# Revit family: BISLEY_CLK_Lockers
name_source: partatom
category: Furniture
revit_build: Autodesk Revit 2018 (Build: 20180423_1000(x64)
units: mm (PartAtom-declared; Revit-internal decimal feet)

## family parameters
Always vertical = Yes
Cut with Voids When Loaded = No
OmniClass Number = 23.40.20.00
OmniClass Title = General Furniture and Specialties
Room Calculation Point = No
Shared = No
Work Plane-Based = No

## types (10) — shared parameters
1st = Yes
5th Door Height = 282 mm
6th Door Height = 282 mm
Category = Furniture
Compliance Standards Certification = BS EN 14073 2004 Part 2 & 3, BS EN 14074, BS 4875 1998 Part 7 level 4, DIN 4554/485
Finish = Powder Coated
Manufacturer = BISLEY
Material = Steel
Model = CLK Lockers
Range = CLK Lockers
Routine Maintenance = We recommend you clean your unit with warm water and a mild detergent solution. A damp cloth can be used to remove dust particles.
URL = www.bisley.com
Uniclass 2015 Code = PR_40_30_48
Uniclass2015Title = Shelves and Storage Units
Uniclass2015Version = V1.1
Warranty = 5 Years from date of purchase
Width = 305 mm  [stored 1.00066 ft]

## per-type parameters (varying)
| type | 1st Door height | 2nd | 2nd Doors Height | 3rd | 3rd Door Height | 4th | 4th Door height | 5th | 6th | Code | Depth | Description | Dimensions | Height | Model Reference | Product Information |
| CLK186 | 282 mm | Yes | 282 mm | Yes | 282 mm | Yes | 282 mm | Yes | Yes |  | 457 mm  [stored 1.49934 ft] | 6 Door Locker | 1802 x 305 x 457 mm | 1802 mm  [stored 5.91207 ft] | CLK186 | 6 Door Locker |
| CLK121 | 1699 mm  [stored 5.57415 ft] | No | 282 mm | No | 282 mm | No | 282 mm | No | No |  | 305 mm  [stored 1.00066 ft] | 1 Door Locker | 529 x 305 x 305 mm | 1802 mm  [stored 5.91207 ft] | CLK121 | 1 Door Locker |
| CLK181 | 1699 mm  [stored 5.57415 ft] | No | 282 mm | No | 282 mm | No | 282 mm | No | No | CLK181 | 457 mm  [stored 1.49934 ft] | 1 Door Locker | 1802 x 305 x 457 mm | 1802 mm  [stored 5.91207 ft] | "CLK181" | 1 Door Locker |
| CLK121C | 426 mm  [stored 1.39764 ft] | No | 282 mm | No | 282 mm | No | 282 mm | No | No |  | 305 mm  [stored 1.00066 ft] |  | 529 x 305 x 305 mm | 529 mm  [stored 1.73556 ft] | CLK121C |  |
| CLK181C | 426 mm  [stored 1.39764 ft] | No | 282 mm | No | 282 mm | No | 282 mm | No | No | CLK181C | 457 mm  [stored 1.49934 ft] | 1 Door Cube | 529 x 305 x 457 mm | 529 mm  [stored 1.73556 ft] | CLK181C | 1 Door Cube |
| CLK122 | 849 mm | Yes | 849 mm | No | 282 mm | No | 282 mm | No | No | CLK122 | 305 mm  [stored 1.00066 ft] | 2 Door Locker | 1802 x 305 x 305 mm | 1802 mm  [stored 5.91207 ft] | CLK122 | 2 Door Locker |
| CLK124 | 424 mm | Yes | 424 mm | Yes | 424 mm | Yes | 424 mm | No | No | CLK124 | 305 mm  [stored 1.00066 ft] | 4 Door Locker | 1802 x 305 x 305 mm | 1802 mm  [stored 5.91207 ft] | CLK124 | 4 Door Locker |
| CLK126 | 282 mm | Yes | 282 mm | Yes | 282 mm | Yes | 282 mm | Yes | Yes | CLK126 | 305 mm  [stored 1.00066 ft] | 6 Door Locker | 1802 x 305 x 305 mm | 1802 mm  [stored 5.91207 ft] | CLK126 | 6 Door Locker |
| CLK182 | 849 mm | Yes | 849 mm | No | 282 mm | No | 282 mm | No | No |  | 457 mm  [stored 1.49934 ft] | 2 Door Locker | 1802 x 305 x 457 mm | 1802 mm  [stored 5.91207 ft] | CLK182 | 2 Door Locker |
| CLK184 | 424 mm | Yes | 424 mm | Yes | 424 mm | Yes | 424 mm | No | No |  | 457 mm  [stored 1.49934 ft] | 4 Door Locker | 1802 x 305 x 457 mm | 1802 mm  [stored 5.91207 ft] | CLK184 | 4 Door Locker |

note: [stored X ft] marks values corroborated as IEEE doubles in the binary element streams (Revit-internal decimal feet)

## geometry (parser evidence)
native form markers: Sweep x1
no freeform markers — native parametric forms only
